# Revit family: 2069359 Sylvania Lighting Fixture PIXER RECESSED 600X600 HE 4P 4000K9 DALI
name_source: partatom
category: Lighting Fixtures
revit_build: Autodesk Revit 2016 (Build: 20150220_1215(x64)
units: mm (PartAtom-declared; Revit-internal decimal feet)

## family parameters
Cut with Voids When Loaded = No
Host = Face
Light Source = No
OmniClass Number = 23.80.70.00
OmniClass Title = Lighting
Part Type = Normal
Room Calculation Point = No
Round Connector Dimension = Use Diameter
Shared = No

## types (1)
- 2069359 PIXER R 600 HE 4P 4K9 DALI
    Apparent Load = 25 VA
    Assembly Code = D5020200
    AssetType = Fixed
    ClassificationName = Uniclass2015
    ClassificationValue = EF_70_80
    Cost = 0 $
    Default Elevation = 1219 mm
    Description = PIXER RECESSED 600X600 HE 4P 4000K9 DALI is a high performance low glare office luminaire with individually adjustable light pods to enhance arhitectural design. Diffuser is made of optical grade polycarbonate with an optical film for high efficacy and excellent glare control. Suitable for offices where aesthetics is important. Ceiling recessed 600x600mm, White colour - RAL9010. DALI dimmable, 4000K Neutral White LED, CRI>90, chromaticity tolerance of 3-step MacAdam ellipse. Lumen package of 3250 lm, total power consumtion 25W, efficacy 130lm/W. Lumen maintenance of L90B10 at 61,000 hours. UGR<19. IK02, IP20. Electrical protection: Class II. Glow wire test 650°C.
    DimmingControlOptions = Dimmable
    DocumentationLiterature = http://www.sylvania-lighting.com
    ElectricShockClassification = Class II
    IfcExportAs = IfcLightFixtureType
    IfcExportType = IfcLightFixtureType
    ImpactProtectionIndex = IK02
    IngressProtection = IP20
    InputNominalFrequency = 50/60 Hz
    InputVoltage = 220-240V~
    Keynote = 16500
    Lamp = LED
    LampColourRenderingIndex = 90
    LampColourTemperature = 4000 K
    LampMacAdamStep = 3
    LampNominalLuminous = 3254 lm
    LampsType = LED
    Length_SYL = 595 mm  [stored 1.9521 ft]
    LightOutputRatio = 100
    LuminousEfficacy = 130 lm/W
    Manufacturer = Feilo Sylvania
    ManufacturerName = Feilo Sylvania
    Material = powder coated steel housing, polycarbonate diffuser
    Material_1_SYL = PC/ABS Plastic
    Model = PIXER RECESSED 600X600 HE 4P 4000K9 DALI
    ModelNumber = 2069359
    ModelReference = PIXER RECESSED 600X600 HE 4P 4000K9 DALI
    Name = PIXER RECESSED 600X600 HE 4P 4000K9 DALI
    NominalDepth = 595 mm  [stored 1.9521 ft]
    NominalHeight = 75 mm
    NominalLength = 595 mm  [stored 1.9521 ft]
    PodXInstance_SYL = 2
    PowerConsumption = 25 W
    PowerFactor = 0
    RadiusBody_SYL = 5 mm  [stored 0.0164042 ft]
    Type Image = <None>
    TypeName = PIXER RECESSED 600X600 HE 4P 4000K9 DALI
    TypePod_SYL = Pixer Pod Square : 2069359 PIXER R 600 HE 4P 4K9 DALI
    URL = http://www.sylvania-lighting.com
    Voltage = 230 V
    Weight = 6.0 kg
    Width_SYL = 595 mm  [stored 1.9521 ft]
    Xdistance_SYL = 149 mm
    Xinstance_SYL = 4
    Ydistance_SYL = 149 mm
    Yinstance_SYL = 4

note: [stored X ft] marks values corroborated as IEEE doubles in the binary element streams (Revit-internal decimal feet)

## geometry (parser evidence)
native form markers: Sweep x4
no freeform markers — native parametric forms only
